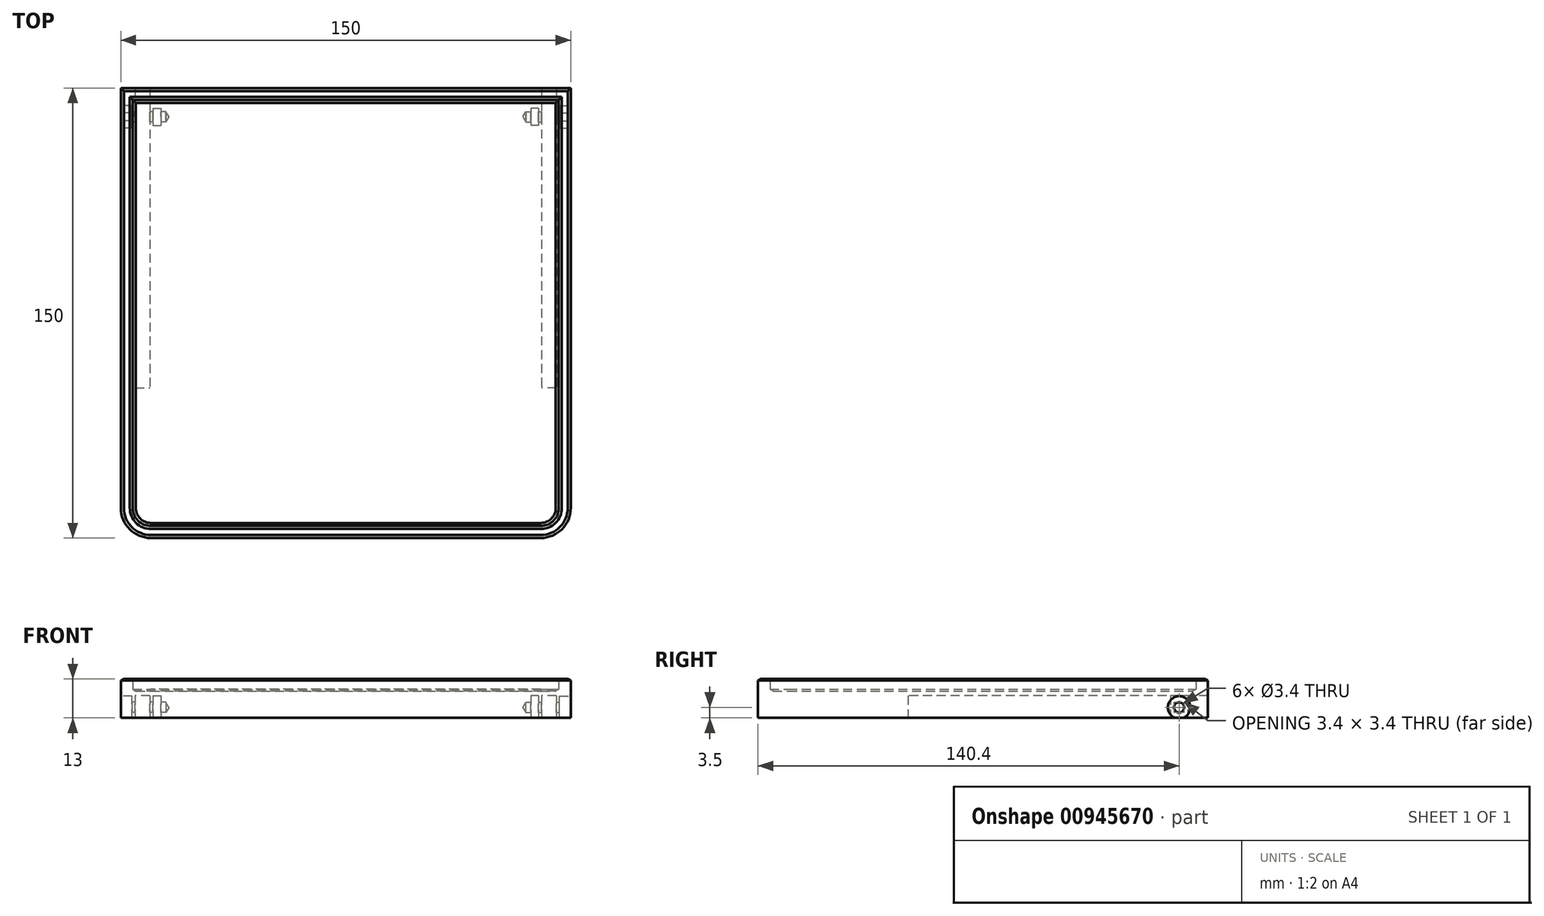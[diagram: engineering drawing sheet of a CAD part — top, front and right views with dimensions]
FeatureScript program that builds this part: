
annotation { "Feature Type Name" : "Feature", "Feature Type Description" : "" }
export const myFeature = defineFeature(function(context is Context, id is Id, definition is map)
    precondition{}
    {
        {
            var Q0;
            Q0=qCreatedBy(makeId("Top.planeOp"),FACE);
            var sketch = newSketch(context, id + "F0", { "sketchPlane" : qUnion([Q0])});
            skLineSegment(sketch, "E0.bottom", {"start": v(75, 75) * mm, "end": v(-75, 75) * mm});
            skLineSegment(sketch, "E0.top", {"start": v(65, -75) * mm, "end": v(-65, -75) * mm});
            skLineSegment(sketch, "E0.left", {"start": v(75, 75) * mm, "end": v(75, -65) * mm});
            skLineSegment(sketch, "E0.right", {"start": v(-75, 75) * mm, "end": v(-75, -65) * mm});
            skPoint(sketch, "E0.middle", {"position": v(0, 0) * mm});
            skPoint(sketch, "E1.visualSharp", {"position": v(-75, -75) * mm});
            skArc(sketch, "E1.filletArc", {"start": v(-75, -65) * mm, "mid": v(-72.07, -72.07) * mm, "end": v(-65, -75) * mm});
            skPoint(sketch, "E2.visualSharp", {"position": v(75, -75) * mm});
            skArc(sketch, "E2.filletArc", {"start": v(65, -75) * mm, "mid": v(72.07, -72.07) * mm, "end": v(75, -65) * mm});
            skSolve(sketch);
        }
        {
            var Q0;
            Q0=makeQuery(id+"F0.imprint","IMPRINT",FACE,{"disambiguationData":[TD([[makeQuery(id+"F0.imprint","IMPRINT",EDGE,{"derivedFrom":sQuery(id+"F0.wireOp",EDGE,"E0.bottom")}),1.0]])]});
            extrude(context, id + "F1", {"entities" : qUnion([Q0]), "depth" : 9 * mm, "offsetDistance" : 25 * mm});
        }
        {
            var Q0;
            Q0=makeQuery(id+"F1.opExtrude","CAP_FACE",FACE,{"disambiguationData":[OSD([sQuery(id+"F0.wireOp",EDGE,"E0.bottom"),sQuery(id+"F0.wireOp",EDGE,"E0.top"),sQuery(id+"F0.wireOp",EDGE,"E0.left"),sQuery(id+"F0.wireOp",EDGE,"E0.right")])],"isStart":true});
            var sketch = newSketch(context, id + "F2", { "sketchPlane" : qUnion([Q0])});
            skLineSegment(sketch, "E3.bottom", {"start": v(70.25, -75) * mm, "end": v(65.25, -75) * mm});
            skLineSegment(sketch, "E3.top", {"start": v(70.25, 25) * mm, "end": v(65.25, 25) * mm});
            skLineSegment(sketch, "E3.left", {"start": v(70.25, -75) * mm, "end": v(70.25, 25) * mm});
            skLineSegment(sketch, "E3.right", {"start": v(65.25, -75) * mm, "end": v(65.25, 25) * mm});
            skLineSegment(sketch, "E4.bottom", {"start": v(64.25, -68.25) * mm, "end": v(61.65, -68.25) * mm});
            skLineSegment(sketch, "E4.top", {"start": v(64.25, -62.55) * mm, "end": v(61.65, -62.55) * mm});
            skLineSegment(sketch, "E4.left", {"start": v(64.25, -68.25) * mm, "end": v(64.25, -62.55) * mm});
            skLineSegment(sketch, "E4.right", {"start": v(61.65, -68.25) * mm, "end": v(61.65, -62.55) * mm});
            skPoint(sketch, "E5", {"position": v(61.65, -65.4) * mm});
            skPoint(sketch, "E6", {"position": v(62.95, -65.4) * mm});
            skPoint(sketch, "E6.positionSnap0", {"position": v(62.95, -68.25) * mm});
            skLineSegment(sketch, "E7", {"start": v(0, -75) * mm, "end": v(0, 0) * mm, "construction": true});
            skLineSegment(sketch, "E8.MirrorCS", {"start": v(-64.25, -62.55) * mm, "end": v(-61.65, -62.55) * mm});
            skLineSegment(sketch, "E9.MirrorCS", {"start": v(-64.25, -68.25) * mm, "end": v(-61.65, -68.25) * mm});
            skLineSegment(sketch, "E10.MirrorCS", {"start": v(-64.25, -68.25) * mm, "end": v(-64.25, -62.55) * mm});
            skLineSegment(sketch, "E11.MirrorCS", {"start": v(-61.65, -68.25) * mm, "end": v(-61.65, -62.55) * mm});
            skPoint(sketch, "E12.MirrorP", {"position": v(-62.95, -65.4) * mm});
            skLineSegment(sketch, "E13.MirrorCS", {"start": v(-70.25, -75) * mm, "end": v(-70.25, 25) * mm});
            skPoint(sketch, "E14.MirrorP", {"position": v(-62.95, -68.25) * mm});
            skLineSegment(sketch, "E15.MirrorCS", {"start": v(-70.25, 25) * mm, "end": v(-65.25, 25) * mm});
            skLineSegment(sketch, "E16.MirrorCS", {"start": v(-70.25, -75) * mm, "end": v(-65.25, -75) * mm});
            skLineSegment(sketch, "E17.MirrorCS", {"start": v(-65.25, -75) * mm, "end": v(-65.25, 25) * mm});
            skPoint(sketch, "E18.MirrorP", {"position": v(-61.65, -65.4) * mm});
            skSolve(sketch);
        }
        {
            var Q0;
            Q0=makeQuery(id+"F2.imprint","IMPRINT",FACE,{"disambiguationData":[TD([[makeQuery(id+"F2.imprint","IMPRINT",EDGE,{"derivedFrom":sQuery(id+"F2.wireOp",EDGE,"E3.bottom")}),-1.0]])]});
            var Q1;
            Q1=makeQuery(id+"F2.imprint","IMPRINT",FACE,{"disambiguationData":[TD([[makeQuery(id+"F2.imprint","IMPRINT",EDGE,{"derivedFrom":sQuery(id+"F2.wireOp",EDGE,"E4.bottom")}),-1.0]])]});
            var Q2;
            Q2=makeQuery(id+"F2.imprint","IMPRINT",FACE,{"disambiguationData":[TD([[makeQuery(id+"F2.imprint","IMPRINT",EDGE,{"derivedFrom":sQuery(id+"F2.wireOp",EDGE,"E8.MirrorCS")}),-1.0]])]});
            var Q3;
            Q3=makeQuery(id+"F2.imprint","IMPRINT",FACE,{"disambiguationData":[TD([[makeQuery(id+"F2.imprint","IMPRINT",EDGE,{"derivedFrom":sQuery(id+"F2.wireOp",EDGE,"E13.MirrorCS")}),-1.0]])]});
            extrude(context, id + "F3", {"entities" : qUnion([Q0, Q1, Q2, Q3]), "operationType" : NewBodyOperationType.REMOVE, "oppositeDirection" : true, "depth" : 7.4 * mm, "offsetDistance" : 25 * mm});
        }
        {
            var Q0;
            Q0=makeQuery(id+"F1.opExtrude","SWEPT_FACE",FACE,{"disambiguationData":[OSD([sQuery(id+"F0.wireOp",EDGE,"E0.right")])]});
            var sketch = newSketch(context, id + "F4", { "sketchPlane" : qUnion([Q0])});
            skPoint(sketch, "E19", {"position": v(-65.4, 3.5) * mm});
            skSolve(sketch);
        }
        {
            var Q0;
            Q0=makeQuery(id+"F1.opExtrude","SWEPT_FACE",FACE,{"disambiguationData":[OSD([sQuery(id+"F0.wireOp",EDGE,"E0.left")])]});
            var sketch = newSketch(context, id + "F5", { "sketchPlane" : qUnion([Q0])});
            skPoint(sketch, "E20", {"position": v(65.4, 3.5) * mm});
            skSolve(sketch);
        }
        {
            var Q0;
            Q0=sQuery(id+"F4.wireOp",VERTEX,"E19");
            var Q1;
            Q1=sQuery(id+"F5.wireOp",VERTEX,"E20");
            var Q2;
            Q2=makeQuery(id+"F1.opExtrude","SWEPT_BODY",BODY,{"disambiguationData":[OSD([sQuery(id+"F0.wireOp",EDGE,"E0.bottom"),sQuery(id+"F0.wireOp",EDGE,"E0.top"),sQuery(id+"F0.wireOp",EDGE,"E0.left"),sQuery(id+"F0.wireOp",EDGE,"E0.right")])]});
            hole(context, id + "F6", {"style" : HoleStyle.C_BORE, "endStyle" : HoleEndStyle.BLIND, "holeDiameter" : 3.4 * mm, "cBoreDiameter" : 7.5 * mm, "cBoreDepth" : 3.75 * mm, "majorDiameter" : 5 * mm, "holeDepth" : 15 * mm, "isTappedThrough" : true, "tappedDepth" : 12 * mm, "tapClearance" : 3, "locations" : qUnion([Q0, Q1]), "scope" : qUnion([Q2])});
        }
        {
            var Q0;
            Q0=makeQuery(id+"F1.opExtrude","CAP_FACE",FACE,{"disambiguationData":[OSD([sQuery(id+"F0.wireOp",EDGE,"E0.bottom"),sQuery(id+"F0.wireOp",EDGE,"E0.top"),sQuery(id+"F0.wireOp",EDGE,"E0.left"),sQuery(id+"F0.wireOp",EDGE,"E0.right"),sQuery(id+"F0.wireOp",EDGE,"E1.filletArc"),sQuery(id+"F0.wireOp",EDGE,"E2.filletArc")])],"isStart":false});
            var sketch = newSketch(context, id + "F7", { "sketchPlane" : qUnion([Q0])});
            skLineSegment(sketch, "E21.0", {"start": v(71, 71) * mm, "end": v(-71, 71) * mm});
            skArc(sketch, "E21.1", {"start": v(-71, -65) * mm, "mid": v(-69.24, -69.24) * mm, "end": v(-65, -71) * mm});
            skLineSegment(sketch, "E21.2", {"start": v(65, -71) * mm, "end": v(-65, -71) * mm});
            skLineSegment(sketch, "E21.3", {"start": v(-71, 71) * mm, "end": v(-71, -65) * mm});
            skArc(sketch, "E21.4", {"start": v(65, -71) * mm, "mid": v(69.24, -69.24) * mm, "end": v(71, -65) * mm});
            skLineSegment(sketch, "E21.5", {"start": v(71, 71) * mm, "end": v(71, -65) * mm});
            skSolve(sketch);
        }
        {
            var Q0;
            Q0=makeQuery(id+"F7.imprint","IMPRINT",FACE,{"disambiguationData":[TD([[makeQuery(id+"F7.imprint","IMPRINT",EDGE,{"derivedFrom":sQuery(id+"F7.wireOp",EDGE,"E21.0")}),-1.0]])]});
            extrude(context, id + "F8", {"entities" : qUnion([Q0]), "operationType" : NewBodyOperationType.ADD, "depth" : 4 * mm, "offsetDistance" : 25 * mm});
        }
        {
            var Q0;
            Q0=makeQuery(id+"F1.opExtrude","CAP_FACE",FACE,{"disambiguationData":[OSD([sQuery(id+"F0.wireOp",EDGE,"E0.bottom"),sQuery(id+"F0.wireOp",EDGE,"E0.top"),sQuery(id+"F0.wireOp",EDGE,"E0.left"),sQuery(id+"F0.wireOp",EDGE,"E0.right"),sQuery(id+"F0.wireOp",EDGE,"E1.filletArc"),sQuery(id+"F0.wireOp",EDGE,"E2.filletArc")])],"isStart":false});
            chamfer(context, id + "F9", {"entities" : qUnion([Q0]), "chamferType" : ChamferType.OFFSET_ANGLE, "width" : 1 * mm, "oppositeDirection" : false, "angle" : 30 * degree, "tangentPropagation" : true});
        }
        {
            var Q0;
            Q0=makeQuery(id+"F8.opExtrude","CAP_EDGE",EDGE,{"disambiguationData":[OSD([sQuery(id+"F7.wireOp",EDGE,"E21.3")])],"isStart":false});
            var Q1;
            Q1=makeQuery(id+"F8.opExtrude","CAP_EDGE",EDGE,{"disambiguationData":[OSD([sQuery(id+"F7.wireOp",EDGE,"E21.0")])],"isStart":false});
            var Q2;
            Q2=makeQuery(id+"F8.opExtrude","CAP_EDGE",EDGE,{"disambiguationData":[OSD([sQuery(id+"F0.wireOp",EDGE,"E0.right")])],"isStart":false});
            var Q3;
            Q3=makeQuery(id+"F8.opExtrude","CAP_EDGE",EDGE,{"disambiguationData":[OSD([sQuery(id+"F0.wireOp",EDGE,"E0.bottom")])],"isStart":false});
            chamfer(context, id + "F10", {"entities" : qUnion([Q0, Q1, Q2, Q3]), "chamferType" : ChamferType.TWO_OFFSETS, "width1" : 0.5 * mm, "oppositeDirection" : false, "width2" : 1 * mm, "tangentPropagation" : true});
        }
    });
